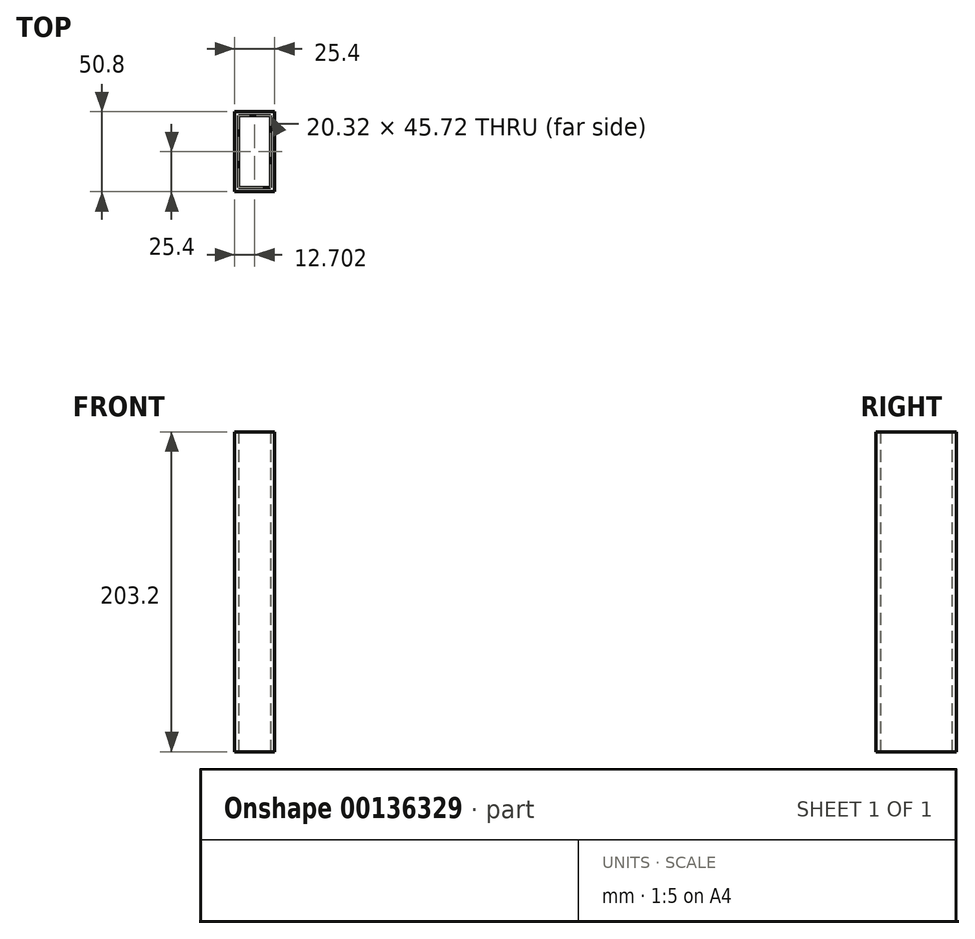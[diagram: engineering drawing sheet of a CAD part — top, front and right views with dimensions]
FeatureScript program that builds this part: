
annotation { "Feature Type Name" : "Feature", "Feature Type Description" : "" }
export const myFeature = defineFeature(function(context is Context, id is Id, definition is map)
    precondition{}
    {
        {
            var Q0;
            Q0=qCreatedBy(makeId("Front.planeOp"),FACE);
            var sketch = newSketch(context, id + "F0", { "sketchPlane" : qUnion([Q0])});
            skLineSegment(sketch, "E0", {"start": v(-18.07, 138.29) * mm, "end": v(-18.07, -64.91) * mm});
            skLineSegment(sketch, "E1", {"start": v(-18.07, 138.29) * mm, "end": v(7.33, 138.29) * mm});
            skLineSegment(sketch, "E2", {"start": v(-18.07, -64.91) * mm, "end": v(7.33, -64.91) * mm});
            skLineSegment(sketch, "E3", {"start": v(7.33, 138.29) * mm, "end": v(7.33, -64.91) * mm});
            skSolve(sketch);
        }
        {
            var Q0;
            Q0 = qSketchRegion(id + "F0", true);
            extrude(context, id + "F1", {"entities" : qUnion([Q0]), "depth" : 50.8 * mm});
        }
        {
            var Q0;
            Q0=makeQuery(id+"F1.opExtrude","SWEPT_FACE",FACE,{"disambiguationData":[OSD([sQuery(id+"F0.wireOp",EDGE,"E1")])]});
            var Q1;
            Q1=makeQuery(id+"F1.opExtrude","SWEPT_FACE",FACE,{"disambiguationData":[OSD([sQuery(id+"F0.wireOp",EDGE,"E2")])]});
            var Q2;
            Q2=makeQuery(id+"F1.opExtrude","SWEPT_BODY",BODY,{"disambiguationData":[OSD([sQuery(id+"F0.wireOp",EDGE,"E0"),sQuery(id+"F0.wireOp",EDGE,"E1"),sQuery(id+"F0.wireOp",EDGE,"E2"),sQuery(id+"F0.wireOp",EDGE,"E3")])]});
            shell(context, id + "F2", {"entities" : qUnion([Q0, Q1]), "parts" : qUnion([Q2]), "thickness" : 2.54 * mm});
        }
    });
